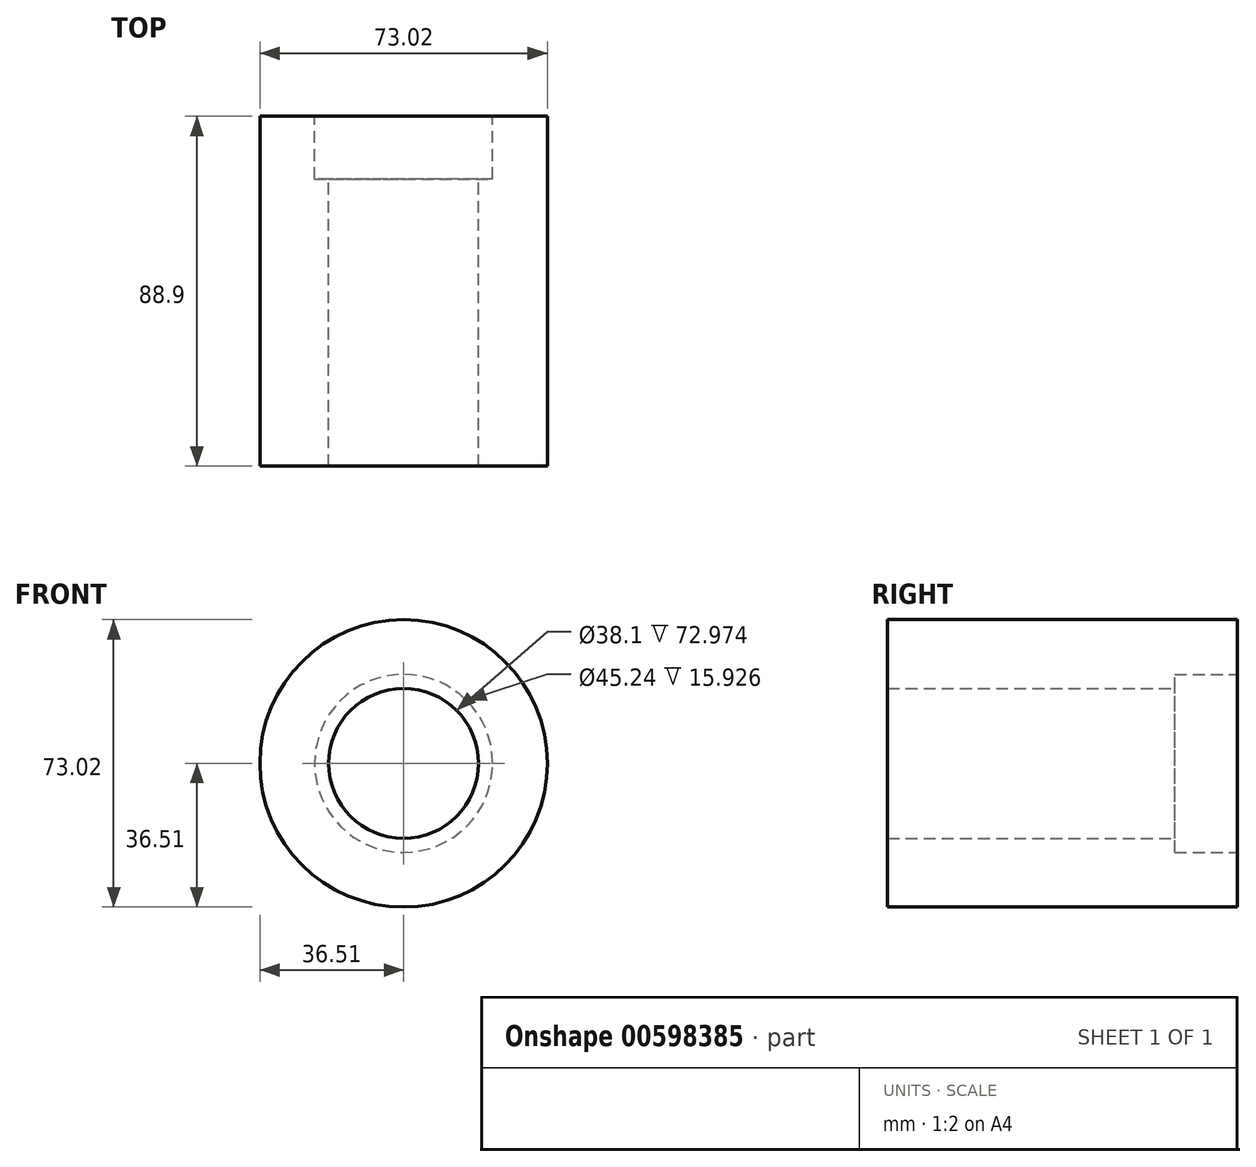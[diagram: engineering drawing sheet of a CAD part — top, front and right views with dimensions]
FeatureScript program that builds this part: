
annotation { "Feature Type Name" : "Feature", "Feature Type Description" : "" }
export const myFeature = defineFeature(function(context is Context, id is Id, definition is map)
    precondition{}
    {
        {
            var Q0;
            Q0=qCreatedBy(makeId("Front.planeOp"),FACE);
            var sketch = newSketch(context, id + "F0", { "sketchPlane" : qUnion([Q0])});
            skCircle(sketch, "E0", {"center": v(0, 0) * mm, "radius": 36.51 * mm});
            skSolve(sketch);
        }
        {
            var Q0;
            Q0 = qSketchRegion(id + "F0", true);
            extrude(context, id + "F1", {"entities" : qUnion([Q0]), "depth" : 88.9 * mm, "offsetDistance" : 25.4 * mm});
        }
        {
            var Q0;
            Q0=qCreatedBy(makeId("Front.planeOp"),FACE);
            var sketch = newSketch(context, id + "F2", { "sketchPlane" : qUnion([Q0])});
            skCircle(sketch, "E1", {"center": v(0, 0) * mm, "radius": 19.05 * mm});
            skSolve(sketch);
        }
        {
            var Q0;
            Q0 = qSketchRegion(id + "F2", true);
            extrude(context, id + "F3", {"entities" : qUnion([Q0]), "operationType" : NewBodyOperationType.REMOVE, "endBound" : BoundingType.THROUGH_ALL, "depth" : 25.4 * mm, "offsetDistance" : 25.4 * mm});
        }
        {
            var Q0;
            Q0=qCreatedBy(makeId("Front.planeOp"),FACE);
            var sketch = newSketch(context, id + "F4", { "sketchPlane" : qUnion([Q0])});
            skCircle(sketch, "E2", {"center": v(0, 0) * mm, "radius": 22.62 * mm});
            skSolve(sketch);
        }
        {
            var Q0;
            Q0 = qSketchRegion(id + "F4", true);
            extrude(context, id + "F5", {"entities" : qUnion([Q0]), "operationType" : NewBodyOperationType.REMOVE, "depth" : 15.93 * mm, "offsetDistance" : 25.4 * mm});
        }
        {
            var Q0;
            Q0=makeQuery(id+"F1.opExtrude","CAP_FACE",FACE,{"disambiguationData":[OSD([sQuery(id+"F0.wireOp",EDGE,"E0")])],"isStart":false});
            cPlane(context, id + "F6", {"entities" : qUnion([Q0]), "cplaneType" : CPlaneType.OFFSET, "offset" : 0 * mm, "width" : 152.4 * mm, "height" : 152.4 * mm});
        }
        {
            var Q0;
            Q0=qCreatedBy(id+"F6.planeOp",FACE);
            var Q1;
            Q1=qCreatedBy(makeId("Front.planeOp"),FACE);
            cPlane(context, id + "F7", {"entities" : qUnion([Q0, Q1]), "cplaneType" : CPlaneType.MID_PLANE, "offset" : 25.4 * mm, "width" : 152.4 * mm, "height" : 152.4 * mm});
        }
    });
